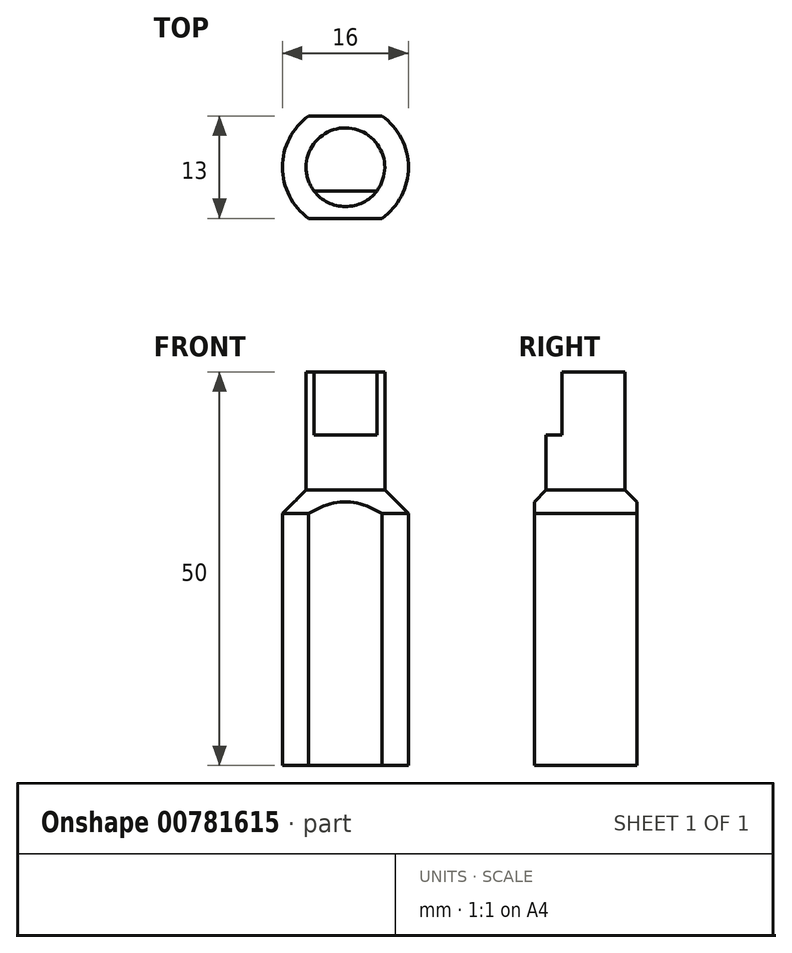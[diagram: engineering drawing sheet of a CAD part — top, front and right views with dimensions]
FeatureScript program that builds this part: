
annotation { "Feature Type Name" : "Feature", "Feature Type Description" : "" }
export const myFeature = defineFeature(function(context is Context, id is Id, definition is map)
    precondition{}
    {
        {
            var Q0;
            Q0=qCreatedBy(makeId("Front.planeOp"),FACE);
            var sketch = newSketch(context, id + "F0", { "sketchPlane" : qUnion([Q0])});
            skLineSegment(sketch, "E0", {"start": v(0, 0) * mm, "end": v(5, 0) * mm});
            skLineSegment(sketch, "E1", {"start": v(5, 0) * mm, "end": v(5, -15) * mm});
            skLineSegment(sketch, "E2", {"start": v(5, -15) * mm, "end": v(8, -18) * mm});
            skLineSegment(sketch, "E3", {"start": v(8, -18) * mm, "end": v(8, -50) * mm});
            skLineSegment(sketch, "E4", {"start": v(8, -50) * mm, "end": v(0, -50) * mm});
            skLineSegment(sketch, "E5", {"start": v(0, -50) * mm, "end": v(0, 0) * mm});
            skSolve(sketch);
        }
        {
            var Q0;
            Q0=makeQuery(id+"F0.imprint","IMPRINT",FACE,{"disambiguationData":[TD([[makeQuery(id+"F0.imprint","IMPRINT",EDGE,{"derivedFrom":sQuery(id+"F0.wireOp",EDGE,"E0")}),-1.0]])]});
            var Q1;
            Q1=sQuery(id+"F0.wireOp",EDGE,"E5");
            revolve(context, id + "F1", {"surfaceOperationType" : NewSurfaceOperationType.NEW, "entities" : qUnion([Q0]), "axis" : qUnion([Q1]), "revolveType" : RevolveType.FULL});
        }
        {
            var Q0;
            Q0=qCreatedBy(makeId("Front.planeOp"),FACE);
            cPlane(context, id + "F2", {"entities" : qUnion([Q0]), "cplaneType" : CPlaneType.OFFSET, "offset" : 3 * mm, "width" : 150 * mm, "height" : 150 * mm});
        }
        {
            var Q0;
            Q0=qCreatedBy(id+"F2.planeOp",FACE);
            var sketch = newSketch(context, id + "F3", { "sketchPlane" : qUnion([Q0])});
            skLineSegment(sketch, "E6.bottom", {"start": v(-10.24, 0) * mm, "end": v(9.76, 0) * mm});
            skLineSegment(sketch, "E6.top", {"start": v(-10.24, -8) * mm, "end": v(9.76, -8) * mm});
            skLineSegment(sketch, "E6.left", {"start": v(-10.24, 0) * mm, "end": v(-10.24, -8) * mm});
            skLineSegment(sketch, "E6.right", {"start": v(9.76, 0) * mm, "end": v(9.76, -8) * mm});
            skSolve(sketch);
        }
        {
            var Q0;
            Q0=makeQuery(id+"F3.imprint","IMPRINT",FACE,{"disambiguationData":[TD([[makeQuery(id+"F3.imprint","IMPRINT",EDGE,{"derivedFrom":sQuery(id+"F3.wireOp",EDGE,"E6.bottom")}),-1.0]])]});
            extrude(context, id + "F4", {"entities" : qUnion([Q0]), "operationType" : NewBodyOperationType.REMOVE, "depth" : 10 * mm, "offsetDistance" : 25 * mm});
        }
        {
            var Q0;
            Q0=qCreatedBy(makeId("Right.planeOp"),FACE);
            var sketch = newSketch(context, id + "F5", { "sketchPlane" : qUnion([Q0])});
            skLineSegment(sketch, "E7.bottom", {"start": v(26.44, 0) * mm, "end": v(6.5, 0) * mm});
            skLineSegment(sketch, "E7.top", {"start": v(26.44, -60) * mm, "end": v(6.5, -60) * mm});
            skLineSegment(sketch, "E7.left", {"start": v(26.44, 0) * mm, "end": v(26.44, -60) * mm});
            skLineSegment(sketch, "E7.right", {"start": v(6.5, 0) * mm, "end": v(6.5, -60) * mm});
            skLineSegment(sketch, "E8.MirrorCS", {"start": v(-6.5, 0) * mm, "end": v(-6.5, -60) * mm});
            skLineSegment(sketch, "E9.MirrorCS", {"start": v(-26.44, 0) * mm, "end": v(-6.5, 0) * mm});
            skLineSegment(sketch, "E10.MirrorCS", {"start": v(-26.44, 0) * mm, "end": v(-26.44, -60) * mm});
            skLineSegment(sketch, "E11.MirrorCS", {"start": v(-26.44, -60) * mm, "end": v(-6.5, -60) * mm});
            skSolve(sketch);
        }
        {
            var Q0;
            Q0 = qSketchRegion(id + "F5", true);
            extrude(context, id + "F6", {"entities" : qUnion([Q0]), "operationType" : NewBodyOperationType.REMOVE, "endBound" : BoundingType.SYMMETRIC, "depth" : 25 * mm, "offsetDistance" : 25 * mm});
        }
    });
